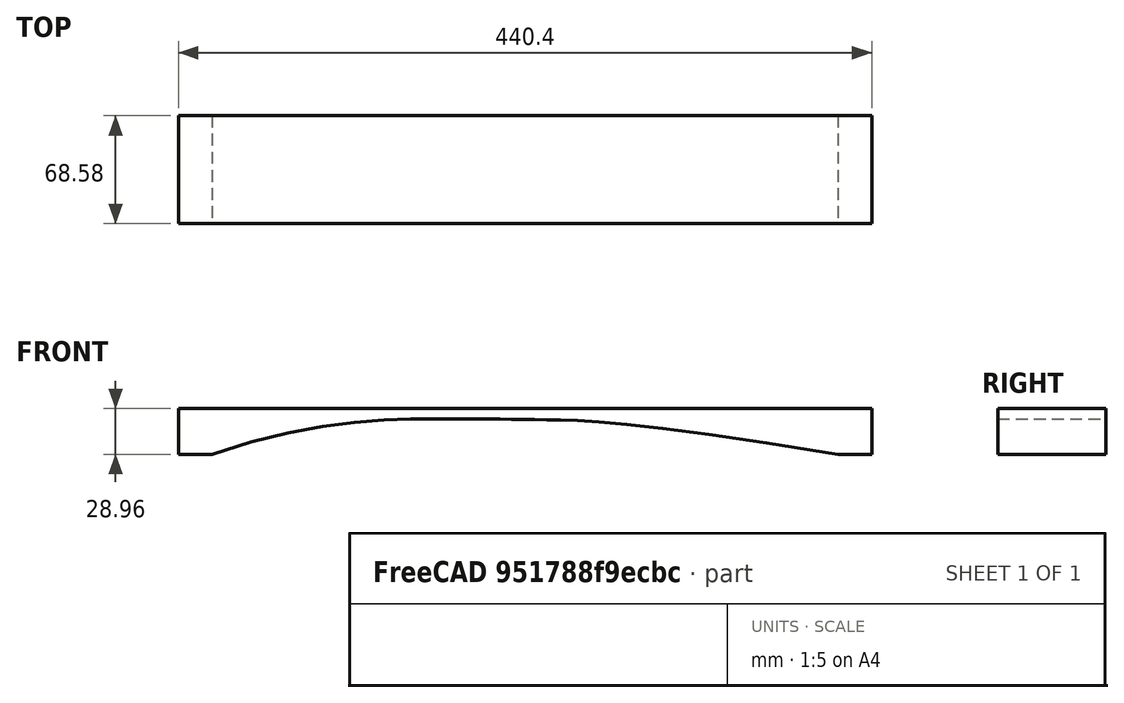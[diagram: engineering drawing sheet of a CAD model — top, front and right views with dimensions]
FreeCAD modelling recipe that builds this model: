
FCSTD DOCUMENT  (FreeCAD 0.20R29410 (Git))
Label: Single_Bar1
License: All rights reserved
LicenseURL: http://en.wikipedia.org/wiki/All_rights_reserved
objects: Fem::FemResultObjectPython×6, Sketcher::SketchObject×1, Part::Extrusion×1, Fem::FemSolverObjectPython×1, App::MaterialObjectPython×1, Fem::ConstraintDisplacement×1, Fem::FemMeshShapeNetgenObject×1, Fem::FemMeshObjectPython×1, App::TextDocument×1, Fem::FemAnalysis×1
note: 2 computed .brp shape members not serialized (recipe doc carries the construction recipe); baked Part::Feature solids carry a one-line shape summary decoded from their .brp

FEATURE [Sketcher::SketchObject] Sketch
  FullyConstrained = true
  Placement = pos=(0,0,0) rot=(1,0,0;1.5708rad)
  sketch-geometry (12):
    g0: LineSegment StartX=21.4 StartY=0 StartZ=0 EndX=0 EndY=0 EndZ=0
    g1: LineSegment StartX=0 StartY=0 StartZ=0 EndX=0 EndY=28.96 EndZ=0
    g2: LineSegment StartX=0 StartY=28.96 StartZ=0 EndX=440.4 EndY=28.96 EndZ=0
    g3: LineSegment StartX=440.4 StartY=28.96 StartZ=0 EndX=440.4 EndY=0 EndZ=0
    g4: LineSegment StartX=440.4 StartY=0 StartZ=0 EndX=419 EndY=0 EndZ=0
    g5-g10: Circle x6 (B-spline internal-alignment scaffolding for g11; pole/knot coordinates omitted)
    g11: BSplineCurve PolesCount=6 KnotsCount=4 Degree=3 IsPeriodic=0
  constraints (38):
    c: DistanceX(g0) = 0
    c: DistanceY(g0) = 0
    c: Distance(g1,g1) = 28.96
    c: Distance(g2,g2) = 440.4
    c: DistanceX(g0,g0) = 21.4
    c: DistanceX(g4,g4) = 21.4
    c: Horizontal(g0)
    c: Vertical(g1)
    c: Horizontal(g2)
    c: Vertical(g3)
    c: Horizontal(g4)
    c: Equal(g3,g1)
    c: Coincident(g0,g1)
    c: Coincident(g1,g2)
    c: Coincident(g2,g3)
    c: Coincident(g3,g4)
    c: DistanceX(g6) = 290.99
    c: DistanceY(g6) = 21.03
    c: DistanceX(g7) = 226.23
    c: DistanceY(g7) = 22.06
    c: DistanceX(g8) = 192.2
    c: DistanceY(g8) = 22.52
    c: DistanceX(g9) = 86.07
    c: DistanceY(g9) = 22.85
    c: Weight(g5) = 1
    c: InternalAlignment(g5,g11)
    c: Weight(g6) = 1
    c: InternalAlignment(g6,g11)
    c: Weight(g7) = 1
    c: InternalAlignment(g7,g11)
    c: Weight(g8) = 1
    c: InternalAlignment(g8,g11)
    c: Weight(g9) = 1
    c: InternalAlignment(g9,g11)
    c: Weight(g10) = 1
    c: InternalAlignment(g10,g11)
    c: Coincident(g4,g11)
    c: Coincident(g0,g11)
FEATURE [Part::Extrusion] Bar
  Base = -> Sketch
  Dir = (0,-1,-3e-16)
  DirMode = 2
  FaceMakerClass = Part::FaceMakerBullseye
  LengthFwd = 68.58
  LengthRev = 0
  Solid = true
  Symmetric = false
FEATURE [Fem::FemSolverObjectPython] SolverCcxTools  # FEM object (typed FeaturePython)
  AnalysisType = 1
  BeamShellResultOutput3D = false
  BucklingFactors = 1
  EigenmodeHighLimit = 20000
  EigenmodeLowLimit = 20
  EigenmodesCount = 12
  GeometricalNonlinearity = 0
  IterationsControlParameterCutb = 0.25,0.5,0.75,0.85,,,1.5,
  IterationsControlParameterIter = 4,8,9,200,10,400,,200,,
  IterationsControlParameterTimeUse = false
  IterationsThermoMechMaximum = 2000
  IterationsUserDefinedIncrementations = false
  IterationsUserDefinedTimeStepLength = false
  MaterialNonlinearity = 0
  MatrixSolverType = 0
  SplitInputWriter = false
  ThermoMechSteadyState = false
  TimeEnd = 1
  TimeInitialStep = 0.01
FEATURE [App::MaterialObjectPython] MaterialSolid  # material (typed FeaturePython)
  Category = 0
  Material = CompressiveStrength=4300 kPa; Density=430 kg/m^3; Name=Wood-Chestnut; PoissonRatio=0.32; ShearModulus=7.4 MPa; UltimateTensileStrength=59.0 MPa; YoungsModulus=8500 MPa
FEATURE [Fem::ConstraintDisplacement] FemConstraintDisplacement
  NormalDirection = (0,3e-16,-1)
  Normals = (110) [(0,3.3e-16,-1),(0,3.3e-16,-1),(0,3.3e-16,-1),(0,3.3e-16,-1),(0,3.3e-16,-1),(0,3.3e-16,-1),(0,3.3e-16,-1),(0,3.3e-16,-1),(0,3.3e-16,-1),(0,3.3e-16,-1),+100 more]
  Points = (110) [(21.4,-68.58,-2.26314e-14),(10.7,-68.58,-2.26314e-14),(0,-68.58,-2.26314e-14),(21.4,-45.72,-1.50876e-14),(10.7,-45.72,-1.50876e-14),+105 more]
  References = -> [Bar]
  rotxFix = false
  rotxFree = true
  rotyFix = false
  rotyFree = true
  rotzFix = false
  rotzFree = true
  xDisplacement = 0
  xFix = false
  xFree = true
  xRotation = 0
  yDisplacement = 0
  yFix = false
  yFree = true
  yRotation = 0
  zDisplacement = 0
  zFix = false
  zFree = true
  zRotation = 0
FEATURE [Fem::FemMeshShapeNetgenObject] FEMMeshNetgen
  Fineness = 4
  GrowthRate = 0.3
  MaxSize = 10
  NbSegsPerEdge = 1
  NbSegsPerRadius = 2
  Optimize = true
  SecondOrder = true
  Shape = -> Bar
FEATURE [Fem::FemMeshObjectPython] ResultMesh  # FEM object (typed FeaturePython)
FEATURE [Fem::FemResultObjectPython] CCX_EigenMode_7_Results  # FEM object (typed FeaturePython)
  DisplacementLengths = [73.6692,73.6675,97.3071,97.3053,92.9945,92.9927,105.905,105.905,112.704,112.704,83.0528,83.0531,92.865,102.962,108.891,106.382,90.7255,75.6183,60.5227,45.387,30.3859,15.6492,4.90783,16.1413,30.7596,45.472,60.0482,74.139,87.5335,99.8965,+5916 more]
  DisplacementVectors = (5946) [(-29.0771,-0.00393964,-67.6881),(-29.0769,0.00473664,-67.6863),(-29.0781,-0.00174479,-92.8608),(-29.0779,0.00241242,-92.859),+5942 more]
  Eigenmode = 7
  EigenmodeFrequency = 127.893
  MaxShear = [0.52739,0.591867,0.0506016,0.0460882,0.0804371,0.098039,0.114135,0.0877355,0.0556531,0.0486395,0.404434,0.419503,0.296947,0.119579,0.178383,0.158839,0.229624,0.660296,1.49302,3.05771,6.05637,10.0987,19.8211,30.5738,45.3514,66.0593,93.6442,+5919 more]
  Mesh = -> ResultMesh
  NodeNumbers = [1,2,3,4,5,6,7,8,9,10,11,12,13,14,15,16,17,18,19,20,21,22,23,24,25,26,27,28,29,30,31,32,33,34,35,36,37,38,39,40,41,42,43,44,45,46,47,48,49,50,51,52,53,54,55,56,57,58,59,60,61,62,63,64,65,66,67,68,69,+5877 more]
  NodeStrainXX = [-0.000119642,-0.000131516,2.52116e-06,2.57943e-06,1.81851e-06,3.90222e-06,3.5195e-07,2.12321e-06,2.36053e-06,2.35781e-06,-8.34904e-05,-8.33955e-05,-5.91647e-05,-1.96769e-05,-7.4614e-06,8.23758e-06,9.19814e-06,0.00010886,0.000271382,+5927 more]
  NodeStrainXY = [1.83996e-05,-1.9545e-05,-1.7626e-06,1.03443e-06,5.54064e-07,-3.24496e-06,-5.29428e-06,4.305e-06,2.33814e-06,-1.72162e-06,-1.79782e-05,1.96224e-05,-2.0511e-05,-5.62808e-06,4.21188e-06,-3.79588e-06,3.11899e-05,5.66166e-05,0.000107873,+5927 more]
  NodeStrainXZ = [3.21037e-06,-1.50244e-05,5.57866e-06,5.33098e-06,9.98465e-06,1.32757e-05,-1.28022e-05,-1.10483e-05,-5.3965e-06,-4.58391e-06,-1.41902e-05,-1.31345e-05,1.46026e-05,9.52499e-06,1.62342e-05,2.01921e-05,1.6494e-05,4.89176e-05,9.8758e-05,+5927 more]
  NodeStrainYY = [3.4399e-05,4.18475e-05,-5.24387e-06,-4.38816e-06,6.40805e-06,2.50142e-06,9.75058e-06,5.85631e-06,-6.33621e-06,-5.57897e-06,2.82298e-05,2.74828e-05,7.81986e-06,2.57164e-06,-8.32709e-06,1.18314e-06,-1.85328e-06,-2.94223e-05,-8.89012e-05,+5927 more]
  NodeStrainYZ = [5.58355e-07,1.00263e-06,2.27123e-06,-2.4793e-06,1.69937e-06,-2.56722e-06,2.70199e-06,-6.16798e-07,3.03519e-06,-3.16863e-06,-7.55747e-06,1.11874e-05,6.30026e-06,7.55929e-06,-1.57843e-05,-1.0551e-05,1.14837e-06,4.00297e-06,-1.18752e-07,+5927 more]
  NodeStrainZZ = [4.17109e-05,4.62749e-05,3.57609e-06,2.83123e-06,-1.13761e-05,-7.69219e-06,-1.26095e-05,-8.24806e-06,4.0092e-06,3.07161e-06,3.11042e-05,3.28491e-05,2.13049e-05,5.00867e-06,1.98025e-05,-9.0146e-06,-2.89223e-06,-4.03627e-05,-8.76131e-05,+5927 more]
  NodeStressXX = [-1.0196,-1.09527,0.0211194,0.0224626,-0.0063175,0.0177524,-0.0120836,0.0121351,0.0153923,0.0143268,-0.675897,-0.669031,-0.552931,-0.195948,-0.0250714,0.0553697,0.0847169,0.924648,2.29055,5.09357,10.1495,17.5392,27.8086,46.7294,74.3148,+5921 more]
  NodeStressXY = [0.118482,-0.125858,-0.01135,0.00666108,0.00356784,-0.0208956,-0.034092,0.0277216,0.0150562,-0.0110862,-0.115769,0.126356,-0.132078,-0.0362414,0.027122,-0.0244432,0.200844,0.364576,0.694634,1.18076,2.10425,3.74355,6.51758,10.023,14.613,+5921 more]
  NodeStressXZ = [0.0206729,-0.0967478,0.0359232,0.0343283,0.0642951,0.0854874,-0.0824386,-0.0711446,-0.0347502,-0.0295176,-0.0913761,-0.0845783,0.0940317,0.0613352,0.104538,0.130025,0.106211,0.315,0.635942,1.09413,2.51491,2.89219,13.6365,18.3075,23.4376,+5921 more]
  NodeStressYY = [-0.027666,0.0210892,-0.0288827,-0.0224044,0.0232363,0.00873208,0.0484379,0.036174,-0.0406095,-0.0367813,0.0435135,0.0449586,-0.121591,-0.0526801,-0.0306459,0.00994338,0.0135524,0.0341973,-0.0294533,-0.0223564,-0.196566,-0.432321,-0.462682,+5923 more]
  NodeStressYZ = [0.00359547,0.00645634,0.0146253,-0.0159652,0.0109429,-0.0165313,0.0173991,-0.0039718,0.0195448,-0.020404,-0.0486655,0.0720403,0.0405699,0.0486773,-0.101641,-0.0679419,0.00739482,0.0257767,-0.000764693,-0.0764151,0.0624407,0.0309516,+5924 more]
  NodeStressZZ = [0.0194184,0.0495988,0.0279125,0.0240841,-0.0912828,-0.0569086,-0.0955478,-0.0546496,0.0260087,0.0189232,0.0620233,0.0795143,-0.0347548,-0.0369871,0.150491,-0.0557239,0.00686225,-0.0362525,-0.021159,-0.0372765,-0.0100599,-0.109105,2.5853,+5923 more]
  PrincipalMax = [0.0208401,0.0666409,0.0607182,0.0582064,0.0345879,0.0831687,0.0820056,0.0746249,0.0561383,0.0469651,0.102327,0.136535,-0.0142484,0.00784923,0.22615,0.163847,0.281082,1.13484,2.62506,5.55164,11.1148,18.7172,34.8505,54.9825,83.7173,124.566,+5920 more]
  PrincipalMed = [-0.014748,0.0258694,-8.4104e-05,-9.41236e-05,0.0173345,-0.00068365,0.00506526,0.0198806,-0.000178905,-0.00018246,0.0338542,0.0213786,-0.0868855,-0.0621556,-0.000761002,-0.000427838,0.00221562,-0.0264947,-0.0241364,0.046074,-0.173919,+5925 more]
  PrincipalMin = [-1.03394,-1.11709,-0.0404849,-0.03397,-0.126286,-0.112909,-0.146264,-0.100846,-0.0551679,-0.0503139,-0.706541,-0.702471,-0.608143,-0.231309,-0.130615,-0.15383,-0.178166,-0.185752,-0.360982,-0.563775,-0.99797,-1.48028,-4.79169,-6.16515,+5922 more]
  ResultType = Fem::ResultMechanical
  Stats = [-29.0786,38.8721,-0.614078,0.614148,-105.797,138.484,1.01682,138.485,0.0483488,534.322,-5.05672,536.125,-45.106,43.424,-533.32,5.80692,0.0277996,268.015,0,0,0,0,0,0,0,0]
  Time = 0
  vonMises = [1.03744,1.16388,0.0882362,0.0807558,0.152979,0.1704,0.201156,0.155502,0.0963963,0.0842593,0.776899,0.787766,0.561113,0.212967,0.312755,0.275171,0.400757,1.2486,2.83268,5.83444,11.7225,19.6064,37.5282,58.521,87.6023,128.655,183.703,252.313,+5918 more]
FEATURE [Fem::FemResultObjectPython] CCX_EigenMode_8_Results  # FEM object (typed FeaturePython)
  DisplacementLengths = [119.986,119.986,118.425,118.426,121.101,121.101,158.735,158.736,166.556,166.557,168.038,168.038,167.542,167.037,153.79,149.763,158.067,157.396,156.692,155.921,155.039,153.958,152.576,150.699,148.092,144.393,139.126,131.843,122.106,109.748,+5916 more]
  DisplacementVectors = (5946) [(-7.21104,47.4306,-109.977),(7.21118,47.4302,109.977),(-7.20026,43.0029,-110.106),(7.20047,43.003,110.107),(-7.05204,-49.9225,-110.107),+5941 more]
  Eigenmode = 8
  EigenmodeFrequency = 439.297
  MaxShear = [6.8768,6.58187,0.632806,0.536714,1.17289,1.33832,1.77202,1.97638,1.05325,1.03926,11.0362,11.2586,7.76355,1.93396,2.65948,2.13644,5.42117,17.6965,32.4332,51.968,77.6808,109.095,147.625,207.062,278.162,363.628,460.209,560.188,653.493,731.262,+5916 more]
  Mesh = -> ResultMesh
  NodeNumbers = <same value as first occurrence — deduplicated (x6 in doc)>
  NodeStrainXX = [0.00147502,-0.00137483,-4.237e-05,4.01089e-05,5.94362e-05,-0.000125532,-0.000118239,0.000232046,7.28825e-05,-7.48978e-05,-0.00236143,0.00240008,-0.0016599,-0.000307137,0.000124711,-0.000120344,0.00104086,0.00397285,0.00746572,0.0119311,+5926 more]
  NodeStrainXY = [0.000256139,0.00032677,-5.96381e-05,-5.15006e-05,6.27801e-05,9.4798e-05,9.09463e-05,0.000166946,-9.95497e-05,-0.000104641,0.000228171,0.000279948,0.000463923,0.000153508,-0.000192135,6.58666e-05,-0.00048798,-0.000698514,-0.000985615,+5927 more]
  NodeStrainXZ = [-0.000366522,0.000420505,9.7992e-06,-4.69516e-06,1.16612e-05,-4.07534e-06,-2.02916e-05,4.3949e-05,-4.85588e-06,1.85302e-05,-0.000783191,0.000799228,-0.000148369,-3.62534e-06,7.77145e-05,0.000153981,-0.00012439,-0.000335253,-0.000537179,+5927 more]
  NodeStrainYY = [-0.000524213,0.00046216,-2.1911e-05,1.94842e-05,8.24434e-05,-4.6769e-05,-8.81564e-05,8.02871e-06,3.16639e-05,-3.19969e-05,0.000832215,-0.000852385,0.000554741,4.45459e-05,0.000201236,-9.38033e-05,-0.000210064,-0.00131068,-0.00238061,+5927 more]
  NodeStrainYZ = [-2.74103e-05,-7.00243e-05,-5.23691e-05,-4.11819e-05,-0.000112998,-9.64257e-05,0.000186304,0.000134041,9.4919e-05,9.06935e-05,7.14911e-05,6.56695e-05,2.91389e-05,0.000157755,-0.00023188,-0.000190993,0.000133404,8.38006e-05,3.83965e-05,+5927 more]
  NodeStrainZZ = [-0.00041494,0.000404234,6.51988e-05,-5.64535e-05,-0.000156871,0.000179907,0.000218563,-0.000205895,-9.71746e-05,8.65484e-05,0.000638462,-0.000657409,0.000499118,4.89714e-05,-0.000304239,0.000273818,-0.00035197,-0.00121193,-0.0023669,+5927 more]
  NodeStressXX = [12.5655,-11.7633,-0.267583,0.276248,0.296923,-0.764811,-0.691746,1.68987,0.511514,-0.598756,-20.3048,20.551,-14.1577,-3.20051,0.927319,-0.433396,9.44331,33.8838,63.6334,101.622,150.013,210.337,259.761,355.381,462.076,575.766,677.793,+5919 more]
  NodeStressXY = [1.64938,2.1042,-0.384033,-0.331633,0.404266,0.610442,0.585639,1.07503,-0.64104,-0.673826,1.46928,1.8027,2.98739,0.988499,-1.23724,0.424141,-3.1423,-4.49801,-6.34676,-9.88515,-18.2624,-29.5205,-54.1298,-83.3151,-123.951,-181.311,-258.465,+5919 more]
  NodeStressXZ = [-2.36018,2.7078,0.0631009,-0.030234,0.0750911,-0.0262427,-0.130665,0.283005,-0.0312689,0.119324,-5.04327,5.14655,-0.955409,-0.023345,0.500435,0.991545,-0.800995,-2.15882,-3.4591,-7.21763,-10.7556,-15.6809,-36.6852,-54.1967,-80.3852,+5921 more]
  NodeStressYY = [-0.308374,0.0658042,-0.13584,0.143438,0.445075,-0.257625,-0.498029,0.247339,0.246092,-0.322501,0.260378,-0.392939,0.103276,-0.935889,1.42009,-0.262488,1.3881,-0.138932,0.229028,0.221337,0.923959,3.14973,3.48502,3.72324,6.00106,9.09407,+5920 more]
  NodeStressYZ = [-0.176506,-0.450914,-0.337225,-0.265186,-0.727638,-0.620923,1.19968,0.863142,0.611221,0.584011,0.46036,0.422872,0.187637,1.01584,-1.49317,-1.22988,0.859039,0.539625,0.24725,0.393437,-0.0313053,0.913457,-4.73871,-7.83643,-10.3208,-12.8632,+5920 more]
  NodeStressZZ = [0.395277,-0.307205,0.425095,-0.345555,-1.09596,1.20203,1.47706,-1.1302,-0.58355,0.440859,-0.987279,0.862587,-0.254906,-0.907392,-1.83486,2.10477,0.474309,0.496955,0.317345,0.427772,-0.106044,-0.478904,-4.68117,-5.81872,-7.1373,-8.48965,+5920 more]
  PrincipalMax = [13.2095,0.430853,0.643733,0.572797,0.931538,1.45734,2.04998,2.39062,1.14005,0.798988,0.422462,21.9684,0.703809,0.237721,2.90281,2.80926,10.6303,34.6116,64.4499,103.085,152.962,215.596,275.115,380.905,504.719,646.75,794.824,926.416,1015.04,+5917 more]
  PrincipalMed = [-0.013016,0.297326,-0.00018087,0.00196622,0.128748,-0.0584483,-0.268626,-0.0214717,0.000446333,0.000139868,0.195806,-0.399028,-0.189855,-1.65131,0.0259041,0.0632434,0.88754,0.411625,0.146473,0.0375826,0.268785,0.0075643,3.58593,5.59854,+5922 more]
  PrincipalMin = [-0.544087,-12.7329,-0.62188,-0.500632,-1.41425,-1.2193,-1.49407,-1.56214,-0.966445,-1.27953,-21.65,-0.548772,-14.8233,-3.63021,-2.41616,-1.46362,-0.212078,-0.781443,-0.416553,-0.851231,-2.39974,-2.59528,-20.1358,-33.2182,-51.6041,-80.5063,+5920 more]
  ResultType = Fem::ResultMechanical
  Stats = [-9.52769,9.53894,-76.8829,53.0045,-149.509,149.508,0.715849,168.038,0.731194,1951.35,-4.00669,1208.44,-31.344,30.6989,-1195.38,5.40699,0.407832,1126.6,0,0,0,0,0,0,0,0]
  Time = 0
  UserDefined = [13.7536,13.1637,1.26561,1.07343,2.34579,2.67663,3.54405,3.95275,2.1065,2.07851,22.0724,22.5172,15.5271,3.86793,5.31897,4.27288,10.8423,35.3931,64.8664,103.936,155.362,218.191,295.251,414.123,556.323,727.256,920.417,1120.38,1306.99,1462.52,+5916 more]
  vonMises = [13.4959,13.0975,1.09611,0.930242,2.06495,2.32482,3.11752,3.4508,1.82633,1.81603,21.96,22.4427,15.1001,3.35003,4.61149,3.75029,10.3365,34.8119,64.5867,103.494,154.045,216.901,284.133,396.144,529.118,686.442,859.815,1032.53,1184.51,1301.8,+5916 more]
FEATURE [Fem::FemResultObjectPython] CCX_EigenMode_9_Results  # FEM object (typed FeaturePython)
  DisplacementLengths = [54.826,54.8154,83.8163,83.8058,82.2506,82.2408,94.1647,94.1621,103.38,103.378,64.9392,64.9376,76.911,90.1383,96.4824,92.7828,72.7188,51.7462,31.946,17.8081,23.8765,41.9659,62.0764,82.3777,101.936,120.086,135.924,148.035,155.01,155.43,+5916 more]
  DisplacementVectors = (5946) [(24.0545,0.0484573,49.2673),(24.0528,-0.053128,49.2563),(24.0678,0.0224879,80.2864),(24.0669,-0.0259825,80.2758),(-17.8669,-0.0257076,80.2866),+5941 more]
  Eigenmode = 9
  EigenmodeFrequency = 517.454
  MaxShear = [7.19366,7.9243,0.645035,0.589606,1.05677,1.2851,1.36954,1.04997,0.64048,0.561347,6.29245,6.44647,4.46465,1.71954,2.09113,1.89825,2.69423,9.49926,20.8265,40.8414,74.7701,118.968,197.289,289.77,403.228,544.669,706.967,872.733,1011.26,1081.85,+5916 more]
  Mesh = -> ResultMesh
  NodeNumbers = <same value as first occurrence — deduplicated (x6 in doc)>
  NodeStrainXX = [0.00164125,0.00177629,-3.08728e-05,-3.13733e-05,-2.93827e-05,-5.29212e-05,1.28785e-05,1.8107e-05,2.48319e-05,2.53805e-05,-0.00133744,-0.00133909,-0.000968663,-0.000329513,-9.15943e-05,9.91222e-05,0.000298276,0.00189847,0.004328,0.00878484,+5926 more]
  NodeStrainXY = [-0.000222711,0.000229767,2.21933e-05,-1.376e-05,-4.51733e-06,3.68019e-05,-5.46873e-05,4.0375e-05,2.55339e-05,-1.83743e-05,-0.00018214,0.000196759,-0.000202327,-6.30377e-05,3.72653e-05,-3.7669e-05,0.000323521,0.000580579,0.00106025,+5927 more]
  NodeStrainXZ = [-6.33551e-05,0.000163835,-7.20874e-05,-6.86863e-05,-0.000131105,-0.000175409,-0.000158099,-0.000139922,-6.43528e-05,-5.47883e-05,-0.000277525,-0.000267383,0.000159465,0.000113773,0.000192218,0.000241678,0.000184488,0.000533279,0.00103712,+5927 more]
  NodeStrainYY = [-0.000485226,-0.000562283,6.61739e-05,5.60823e-05,-8.1851e-05,-3.15787e-05,0.000111921,6.85868e-05,-7.11427e-05,-6.29853e-05,0.000457357,0.000449601,0.000195339,7.0874e-05,-9.77664e-05,1.79344e-05,-8.84041e-05,-0.000557485,-0.00141145,+5927 more]
  NodeStrainYZ = [4.93019e-07,-1.58631e-05,-2.72614e-05,3.03896e-05,-1.76138e-05,2.8339e-05,2.51152e-05,-4.08648e-06,3.18281e-05,-3.47276e-05,-8.79435e-05,0.000126475,5.9735e-05,7.6048e-05,-0.000176666,-0.000121083,7.88856e-06,2.99812e-05,-1.90956e-05,+5927 more]
  NodeStrainZZ = [-0.000565771,-0.000626256,-4.78106e-05,-3.84883e-05,0.000155529,0.000104951,-0.000163657,-0.000100407,5.04993e-05,3.87813e-05,0.000467652,0.000487903,0.000334966,8.8635e-05,0.000254418,-0.00012134,-9.42359e-05,-0.00066772,-0.00138982,+5927 more]
  NodeStressXX = [13.9472,14.8025,-0.270406,-0.280897,0.0643377,-0.223722,-0.139489,0.0381034,0.183877,0.170169,-10.973,-10.9216,-8.74673,-3.09495,-0.217429,0.613772,2.58261,16.0788,36.6085,74.4322,136.325,221.62,323.184,501.096,730.944,1022.68,1364.09,+5919 more]
  NodeStressXY = [-1.43413,1.47956,0.142911,-0.0886062,-0.0290889,0.236982,-0.352153,0.259991,0.164423,-0.118319,-1.17287,1.26701,-1.30286,-0.405924,0.239966,-0.242566,2.08328,3.73857,6.82735,11.0372,18.2412,30.2147,49.3568,69.3973,91.561,111.767,123.754,+5919 more]
  NodeStressXZ = [-0.407969,1.055,-0.464199,-0.442298,-0.844236,-1.12953,-1.01806,-0.901014,-0.414393,-0.352803,-1.78709,-1.72179,1.02686,0.732628,1.23777,1.55626,1.18799,3.43399,6.67844,10.7305,23.8866,24.9251,116.425,143.467,165.513,180.804,180.279,157.12,+5918 more]
  NodeStressYY = [0.254001,-0.256529,0.354516,0.282264,-0.273526,-0.0862886,0.498284,0.363163,-0.434141,-0.398853,0.584389,0.596496,-1.25126,-0.516702,-0.257173,0.0909718,0.0926212,0.263866,-0.349998,-0.371983,-1.65969,-3.80126,-1.78117,-1.97116,0.288604,+5921 more]
  NodeStressYZ = [0.00317475,-0.102149,-0.175547,0.195691,-0.113422,0.182486,0.161727,-0.0263144,0.204954,-0.223624,-0.566303,0.814424,0.384657,0.489703,-1.13762,-0.779702,0.0507976,0.193061,-0.122964,-0.853303,0.220227,0.000548324,4.20607,5.6384,6.57102,+5921 more]
  NodeStressZZ = [-0.26466,-0.668477,-0.379475,-0.326713,1.25506,0.792879,-1.27627,-0.725057,0.349159,0.256462,0.650681,0.843138,-0.352148,-0.402331,2.01068,-0.805869,0.0550679,-0.445978,-0.210705,-0.3745,-0.196789,-1.4965,22.6644,16.8128,17.9026,16.772,+5920 more]
  PrincipalMax = [14.1073,15.0155,0.496542,0.425913,1.69662,1.52359,0.864573,0.769108,0.691873,0.577568,1.21377,1.56675,-0.17001,0.0637587,2.85868,1.84735,4.04908,17.5581,38.9276,77.4443,142.635,228.258,369.242,548.909,778.099,1065.88,1398.76,1738.28,+5918 more]
  PrincipalMed = [0.109332,-0.304881,0.00162204,0.0020387,-0.23384,0.00588034,0.0924651,0.23794,-0.00389054,-0.00466526,0.419425,0.277473,-1.08081,-0.702426,0.000990845,0.00065943,0.0206089,-0.220924,-0.154243,0.479818,-1.26129,-2.25876,0.159718,-2.33964,+5922 more]
  PrincipalMin = [-0.280056,-0.833109,-0.793529,-0.753298,-0.41691,-1.04661,-1.87451,-1.33084,-0.589087,-0.545125,-11.3711,-11.3262,-9.09932,-3.37532,-1.32359,-1.94914,-1.33939,-1.44045,-2.72553,-4.2384,-6.90519,-9.67706,-25.3349,-30.6317,-28.3568,-23.4602,+5920 more]
  ResultType = Fem::ResultMechanical
  Stats = [-17.8701,46.0124,-1.86934,1.86731,-116.978,156.053,0.831568,156.224,0.622299,2147.23,-24.9315,2161.96,-330.761,318.014,-2144.3,32.6406,0.356801,1085.5,0,0,0,0,0,0,0,0]
  Time = 0
  vonMises = [14.1966,15.5912,1.12727,1.03459,2.0282,2.23798,2.4462,1.89116,1.11072,0.972505,12.2071,12.2991,8.51054,3.12719,3.70218,3.28826,4.85354,18.4191,40.4288,79.4288,146.8,234.314,382.468,565.925,792.945,1077.26,1404.36,1736.34,2008.35,2143.76,+5916 more]
FEATURE [Fem::FemResultObjectPython] CCX_EigenMode_10_Results  # FEM object (typed FeaturePython)
  DisplacementLengths = [76.2192,76.2182,98.9648,98.9639,115.566,115.566,128.799,128.798,102.171,102.168,79.835,79.8335,86.7825,94.4275,109.813,118.659,116.197,104.071,92.5148,81.7473,72.2181,64.3434,58.7281,55.8455,55.9688,58.8698,64.0466,70.8439,78.7046,87.0527,+5916 more]
  DisplacementVectors = (5946) [(44.4024,57.8037,22.283),(-44.401,57.8039,-22.2816),(44.4139,85.5424,22.4483),(-44.4132,85.5423,-22.4463),(44.1858,104.397,22.4577),+5941 more]
  Eigenmode = 10
  EigenmodeFrequency = 1114.62
  MaxShear = [7.02165,7.3129,0.625801,0.522768,3.29847,4.47889,4.95916,5.63025,1.36168,1.38004,9.65909,10.4723,7.34647,4.69604,3.10374,5.60564,14.3619,53.323,105.029,173.904,262.269,364.688,496.131,648.998,814.437,986.97,1153.82,1298.77,1413.38,1501.29,+5916 more]
  Mesh = -> ResultMesh
  NodeNumbers = <same value as first occurrence — deduplicated (x6 in doc)>
  NodeStrainXX = [0.00136374,-0.00145839,4.62407e-05,-4.53288e-05,-0.000192482,0.000382576,-0.000336682,0.000673931,0.000123602,-0.000129686,-0.00184741,0.00195683,-0.00110578,0.000100109,0.000116055,-0.000380575,0.00309335,0.0121943,0.0244241,0.0405467,+5926 more]
  NodeStrainXY = [-0.00052207,-0.000384411,-3.04978e-05,-6.23019e-06,-0.000271578,-0.000504267,0.000383017,0.000557847,-6.05385e-05,-8.72441e-05,0.000579255,0.000678504,0.000885837,0.000625294,-9.98436e-05,0.000262202,-0.000740143,-0.00136898,-0.0021695,+5927 more]
  NodeStrainXZ = [3.69665e-05,-0.000220017,3.46429e-05,-5.07515e-05,-3.26497e-05,1.40395e-05,-2.27621e-05,7.54134e-05,-6.62314e-05,9.95628e-05,-0.000768293,0.000837972,-0.000298431,-0.000118687,0.000107478,0.00029065,-0.000196906,-0.000808819,-0.00126852,+5927 more]
  NodeStrainYY = [-0.000461521,0.000439887,-8.05557e-05,5.1194e-05,-0.000251186,0.00021801,-0.000301738,8.67145e-05,-7.35616e-05,5.71523e-05,0.000660458,-0.000705623,0.000242361,-0.000212833,5.36063e-05,-0.000339461,-0.000778218,-0.00405338,-0.00784809,+5927 more]
  NodeStrainYZ = [0.000113862,0.00010933,6.69562e-05,4.01166e-05,0.000213106,0.000188128,0.000401769,0.000288184,0.000156709,0.000136404,0.000179096,0.000161646,0.000138601,0.000333274,-0.000435484,-0.000335376,0.000276418,0.000198045,0.000124466,+5927 more]
  NodeStrainZZ = [-0.000495117,0.00059468,-7.6909e-08,-8.56089e-06,0.00042922,-0.000496782,0.000604714,-0.000588935,-6.43117e-05,4.17856e-05,0.000416193,-0.000477758,0.000360339,-8.4078e-05,-0.000175345,0.000875315,-0.00101856,-0.00377454,-0.00776179,+5927 more]
  NodeStressXX = [11.1119,-11.8171,0.100906,-0.307319,-1.32217,3.05772,-2.36096,5.32256,0.714234,-1.0111,-16.3079,17.028,-10.0001,-0.48183,0.714789,-1.56187,27.3407,103.517,207.728,345.152,519.998,724.208,956.915,1249.88,1564.25,1890.88,2207.13,2485.68,+5918 more]
  NodeStressXY = [-3.36181,-2.47537,-0.196387,-0.0401187,-1.7488,-3.24717,2.4664,3.5922,-0.389831,-0.561799,3.73005,4.36915,5.70425,4.02652,-0.642932,1.68842,-4.76607,-8.81539,-13.9703,-19.8182,-33.5159,-49.697,-86.0763,-119.751,-159.054,-203.334,-247.582,+5919 more]
  NodeStressXZ = [0.238042,-1.41678,0.223079,-0.326809,-0.210244,0.0904056,-0.146574,0.485616,-0.42649,0.641124,-4.94734,5.39603,-1.92171,-0.76427,0.692094,1.87161,-1.26796,-5.2083,-8.16851,-15.2356,-21.8907,-26.7799,-70.8296,-92.5163,-120.826,-152.009,+5920 more]
  NodeStressYY = [-0.641692,0.406682,-0.715585,0.314229,-1.70019,1.99802,-2.13594,1.54124,-0.55538,0.192026,-0.158793,-0.11661,-1.3189,-2.49699,0.312658,-1.29712,2.41016,-1.10856,-0.0852899,0.621013,1.35149,5.95576,2.58203,2.18296,2.04041,1.22315,-1.16515,+5919 more]
  NodeStressYZ = [0.733205,0.704019,0.431157,0.258327,1.37227,1.21143,2.58715,1.85573,1.00911,0.878357,1.15327,1.04091,0.892503,2.14608,-2.80426,-2.15962,1.77997,1.27529,0.801482,1.48392,1.0302,2.2151,-4.2851,-7.26027,-9.29572,-10.9766,-11.7121,-11.099,+5918 more]
  NodeStressZZ = [-0.858031,1.40345,-0.197351,-0.0705565,2.68122,-2.60481,3.70106,-2.80953,-0.495816,0.0930745,-1.73171,1.3507,-0.559195,-1.66789,-1.16165,6.5253,0.86248,0.68699,0.470444,0.95816,-0.333561,0.27912,-11.2458,-11.5452,-13.1857,-13.5665,-12.5061,+5919 more]
  PrincipalMax = [12.0057,2.21171,0.221835,0.492135,3.19237,5.87941,4.76746,7.67533,1.18807,1.02294,0.665485,19.7184,1.51008,2.79324,2.87724,7.31247,28.3109,104.525,208.986,346.964,523.072,728.622,969.636,1267.8,1589.16,1924.13,2248.61,2532.48,2761.38,+5917 more]
  PrincipalMed = [-0.355822,0.195418,-0.00409808,-0.00238057,-0.128931,-0.350109,-0.412436,-0.0358974,0.0102602,-0.0117948,-0.211191,-0.229956,-0.20542,-0.841127,0.318788,0.252653,2.71538,0.691884,0.200542,0.611094,-0.589868,2.57506,1.24156,2.90956,3.65638,+5921 more]
  PrincipalMin = [-2.03765,-12.4141,-1.02977,-0.553401,-3.40458,-3.07837,-5.15086,-3.58517,-1.53529,-1.73714,-18.6527,-1.22633,-13.1829,-6.59883,-3.33023,-3.89881,-0.412917,-2.12119,-1.07311,-0.844319,-1.4664,-0.753685,-22.6266,-30.194,-39.7127,-49.8148,+5920 more]
  ResultType = Fem::ResultMechanical
  Stats = [-49.9118,49.9103,-123.773,112.619,-38.2598,38.2643,0.528405,128.799,0.905902,4115.61,-15.4734,4118.61,-109.569,119.045,-4119.73,11.3021,0.522768,2059.8,0,0,0,0,0,0,0,0]
  Time = 0
  vonMises = [13.2825,13.7292,1.15533,0.905902,5.71317,7.95275,8.59235,9.97144,2.36566,2.41511,18.8951,20.4647,13.9147,8.20277,5.40341,9.81755,27.2944,105.268,209.425,347.083,524.101,727.717,980.547,1281.77,1607.63,1947.48,2276.84,2564.54,2794.3,2973.12,+5916 more]
FEATURE [Fem::FemResultObjectPython] CCX_EigenMode_11_Results  # FEM object (typed FeaturePython)
  DisplacementLengths = [48.4227,48.399,79.1734,79.1499,75.4207,75.3971,78.4911,78.4832,86.9854,86.9798,51.5983,51.5964,61.9331,74.2566,79.4823,75.8705,57.6304,37.9274,22.5145,22.9682,38.3324,56.9849,75.295,91.6826,104.398,111.357,109.928,97.4125,71.9486,34.2871,+5916 more]
  DisplacementVectors = (5946) [(29.7097,0.247689,38.2365),(29.7056,-0.264639,38.2095),(29.7889,0.111854,73.3556),(29.7891,-0.126206,73.3301),(-17.522,-0.136126,73.357),+5941 more]
  Eigenmode = 11
  EigenmodeFrequency = 1285.6
  MaxShear = [41.768,45.2412,3.379,3.09644,5.68449,6.8853,6.29792,4.82474,2.87575,2.52241,33.1101,33.7703,23.3186,8.85674,9.52198,8.73981,13.0541,49.1863,104.856,199.003,346.148,531.1,786.271,1098.22,1428.32,1771.17,2059.55,2189.5,2050.51,1597.22,969.4,+5915 more]
  Mesh = -> ResultMesh
  NodeNumbers = <same value as first occurrence — deduplicated (x6 in doc)>
  NodeStrainXX = [0.00957121,0.01023,-0.000156458,-0.000158053,-0.000181278,-0.000297808,-8.61308e-05,-6.74878e-05,-0.000103791,-0.000107901,0.00709724,0.00711186,0.00519362,0.00178952,0.000426737,-0.000456634,-0.00193903,-0.0104,-0.0227476,-0.0441477,+5926 more]
  NodeStrainXY = [-0.00112608,0.00113329,0.000114673,-7.39034e-05,-1.36066e-05,0.000176806,0.000227251,-0.000154609,-0.000110771,7.82676e-05,0.000748625,-0.000803003,0.000814811,0.000280452,-0.000135528,0.00015257,-0.00135664,-0.00240411,-0.00422875,+5927 more]
  NodeStrainXZ = [-0.000486776,0.000694915,-0.000381376,-0.000362293,-0.000701,-0.000941564,0.000737394,0.000661158,0.000295222,0.000251498,0.00156736,0.00152775,-0.000694253,-0.000526276,-0.000881627,-0.00111463,-0.00082025,-0.00231578,-0.00435483,+5927 more]
  NodeStrainYY = [-0.00289296,-0.0032352,0.000343909,0.000294196,-0.000429069,-0.000161157,-0.000499506,-0.000309451,0.000314103,0.00027882,-0.00243723,-0.00240463,-0.00118513,-0.000441219,0.000444421,-9.09546e-05,0.000603856,0.00313965,0.00740538,0.0142604,+5926 more]
  NodeStrainYZ = [3.4844e-05,-9.70835e-05,-0.000136707,0.000154907,-7.68213e-05,0.000132931,-9.59194e-05,9.69386e-06,-0.000133922,0.000150705,0.000395931,-0.000558912,-0.000232823,-0.000311318,0.000781794,0.000544295,-2.08781e-05,-9.07972e-05,0.000126872,+5927 more]
  NodeStrainZZ = [-0.00326348,-0.00359382,-0.000259111,-0.000211099,0.000857892,0.000579112,0.00078701,0.00046761,-0.000239608,-0.000184564,-0.0024172,-0.00250797,-0.00176676,-0.000490797,-0.00121659,0.00059045,0.000613179,0.00358327,0.00728248,0.0141811,+5926 more]
  NodeStressXX = [81.1786,85.3422,-1.41767,-1.44681,0.2496,-1.22999,0.59801,0.0844118,-0.836042,-0.772913,58.5396,58.3844,46.2752,16.4318,0.770713,-2.69511,-16.6188,-88.0166,-192.613,-374.185,-652.171,-1017.06,-1399.42,-2030.92,-2737.23,-3472.11,-4087.1,+5919 more]
  NodeStressXY = [-7.25126,7.29771,0.738423,-0.475893,-0.0876185,1.13853,1.46336,-0.995587,-0.713296,0.503996,4.82069,-5.17085,5.24689,1.80594,-0.872718,0.982459,-8.73596,-15.481,-27.2306,-42.1359,-64.7517,-99.1896,-150.712,-188.355,-213.294,-206.342,+5920 more]
  NodeStressXZ = [-3.13454,4.47483,-2.45583,-2.33295,-4.51402,-6.0631,4.74837,4.25745,1.90105,1.6195,10.0929,9.83777,-4.47057,-3.3889,-5.67714,-7.17751,-5.28191,-14.9122,-28.0425,-42.6842,-91.5367,-87.0676,-395.949,-440.683,-440.742,-391.047,-270.276,+5919 more]
  NodeStressYY = [0.916897,-1.36569,1.80438,1.4654,-1.34602,-0.350039,-2.06388,-1.47369,1.85494,1.71733,-2.85662,-2.89596,5.1999,2.06712,0.88459,-0.340354,-0.244133,-0.829649,1.55325,1.92716,5.58847,13.2627,-0.941604,-4.11195,-17.4149,-35.0507,-56.7481,+5919 more]
  NodeStressYZ = [0.224374,-0.625159,-0.880308,0.997506,-0.494682,0.855992,-0.617663,0.0624226,-0.862379,0.97045,2.54955,-3.59906,-1.49924,-2.0047,5.03428,3.50493,-0.134442,-0.584679,0.816981,3.63921,0.167652,0.862896,-15.3184,-17.836,-18.7001,-19.0526,+5920 more]
  NodeStressZZ = [-1.46908,-3.67498,-2.0787,-1.78839,6.94123,4.41685,6.22051,3.53012,-1.71062,-1.26658,-2.72764,-3.56141,1.4546,1.74786,-9.81132,4.04748,-0.184098,2.02697,0.761857,1.41685,0.675727,6.86657,-79.065,-48.9985,-44.1103,-30.2427,-10.1778,12.4548,+5918 more]
  PrincipalMax = [81.9468,86.1683,2.52645,2.20446,9.22953,8.28312,8.93071,6.43265,2.51638,2.34639,60.5801,60.4164,47.4001,17.4913,5.46166,9.2525,4.57129,5.38399,9.5398,14.5668,21.4537,28.4712,48.8385,55.414,32.8705,14.075,8.65848,16.2611,36.5258,83.5763,+5916 more]
  PrincipalMed = [0.268748,-1.55271,0.0131155,0.0141539,-1.24527,0.0411952,-0.51094,-1.07498,0.0270233,0.0298739,-1.98455,-1.36508,4.76669,2.97761,-0.0353935,-0.0133637,-0.0813314,0.785267,0.334112,-1.96899,3.48219,8.32647,-4.56193,1.5775,-7.8463,-23.2112,+5920 more]
  PrincipalMin = [-1.58914,-4.3141,-4.23156,-3.98841,-2.13945,-5.48749,-3.66513,-3.21683,-3.23513,-2.69843,-5.64019,-7.12424,0.762876,-0.222154,-13.5823,-8.22712,-21.537,-92.9885,-200.172,-383.439,-670.843,-1033.73,-1523.7,-2141.02,-2823.78,-3528.27,+5920 more]
  ResultType = Fem::ResultMechanical
  Stats = [-42.6844,29.8253,-3.92765,3.93459,-111.863,213.263,0.806372,213.294,3.7953,4746.69,-82.9821,4792.26,-782.611,801.399,-4729.42,88.0078,2.17473,2400.21,0,0,0,0,0,0,0,0]
  Time = 0
  vonMises = [82.6227,89.1338,5.91628,5.43919,10.9493,12.0026,11.3523,8.7768,4.99592,4.37379,64.4702,64.8531,44.7698,16.3501,16.9766,15.1469,24.1209,96.1557,205.264,390.001,683.488,1052.27,1546.53,2170.02,2836.51,3523.85,4089,4332.42,4044.61,3134.2,+5916 more]
FEATURE [Fem::FemResultObjectPython] CCX_EigenMode_12_Results  # FEM object (typed FeaturePython)
  DisplacementLengths = [68.6825,68.6794,70.4286,70.4376,62.2603,62.2696,66.2944,66.2941,73.2368,73.2388,72.2587,72.2605,72.6775,73.0023,66.9255,63.9525,65.5463,64.6471,63.4084,61.6079,58.9394,54.847,48.7559,39.6913,26.9666,14.558,30.4436,67.1448,115.21,171.456,+5916 more]
  DisplacementVectors = (5946) [(1.10693,34.6241,-59.3062),(-1.10197,34.6194,59.3055),(1.21312,36.0292,-60.503),(-1.20752,36.0299,60.5132),(2.56965,-14.4649,-60.5021),+5941 more]
  Eigenmode = 12
  EigenmodeFrequency = 1821.99
  MaxShear = [67.1035,64.1939,6.14657,5.20353,10.3253,11.4864,12.4372,13.7859,7.61105,7.48886,77.498,79.0024,54.6978,13.3493,19.2994,14.8891,37.9595,120.846,217.894,342.827,500.732,684.832,919.199,1245.45,1607.5,2001.08,2387.35,2713.8,2940.91,3064.92,+5916 more]
  Mesh = -> ResultMesh
  NodeNumbers = <same value as first occurrence — deduplicated (x6 in doc)>
  NodeStrainXX = [0.0144731,-0.0135291,-0.000392336,0.000370678,0.000515251,-0.00109016,0.00082505,-0.00160861,-0.000516915,0.000531286,0.0165749,-0.0168349,0.0116519,0.00211934,-0.000922977,0.000845393,-0.00720032,-0.0270294,-0.0500085,-0.0783699,-0.112641,+5925 more]
  NodeStrainXY = [0.00232406,0.00304784,-0.000592495,-0.000504406,0.000511325,0.000739536,-0.000619302,-0.00115243,0.000725651,0.000758347,-0.00160892,-0.00197214,-0.00328866,-0.00104456,0.00139585,-0.000452104,0.00352734,0.00500637,0.00700461,0.0108467,+5926 more]
  NodeStrainXZ = [-0.00351119,0.00400049,0.000116646,-7.23887e-05,0.000120368,-6.03623e-05,0.000116057,-0.000283473,1.73874e-05,-0.000114408,0.00549988,-0.00560777,0.0010604,2.4041e-05,-0.000531154,-0.00105871,0.000909471,0.00241123,0.00388731,0.00797089,+5926 more]
  NodeStrainYY = [-0.00514722,0.00453861,-0.000249434,0.000214947,0.000722307,-0.00038359,0.000628396,-6.23541e-05,-0.000251112,0.000250469,-0.00584607,0.00598528,-0.00393178,-0.000311908,-0.00148562,0.000646403,0.00142925,0.00892137,0.0159357,0.0250669,+5926 more]
  NodeStrainYZ = [-0.000226324,-0.000638746,-0.000482633,-0.000382792,-0.00102012,-0.000866938,-0.00131218,-0.000945517,-0.000673168,-0.00064396,-0.000510676,-0.000476265,-0.000190016,-0.0011071,0.00163092,0.00134563,-0.000940463,-0.000573007,-0.000263743,+5927 more]
  NodeStrainZZ = [-0.00409521,0.00401858,0.000641025,-0.000558262,-0.0013961,0.0015902,-0.00155866,0.00145163,0.000714867,-0.000638234,-0.00446849,0.00459314,-0.00348794,-0.000324141,0.00227182,-0.00191073,0.00243889,0.00822119,0.015845,0.0248417,0.0363973,+5925 more]
  NodeStressXX = [123.138,-115.578,-2.53066,2.54356,2.41043,-6.35337,4.71057,-11.6139,-3.6329,4.24267,142.566,-144.218,99.2563,22.1375,-6.72627,3.04585,-65.4388,-230.644,-426.359,-667.564,-959.482,-1307.43,-1549.69,-2022.58,-2471.58,-2825.02,-2925.38,+5919 more]
  NodeStressXY = [14.9656,19.6263,-3.81531,-3.24807,3.29262,4.76217,-3.98793,-7.42094,4.67275,4.8833,-10.3605,-12.6994,-21.177,-6.7263,8.98843,-2.91128,22.7139,32.238,45.1054,69.8462,127.352,203.293,365.939,550.309,794.842,1118.04,1514.48,1946.31,2333.99,+5917 more]
  NodeStressXZ = [-22.6099,25.7608,0.751129,-0.466139,0.775099,-0.388696,0.747338,-1.82539,0.111965,-0.73672,35.4159,-36.1106,6.82831,0.15481,-3.42031,-6.81748,5.85644,15.5268,25.0319,51.3277,78.55,111.046,280.542,405.63,580.262,804.012,1070.49,1343.69,+5918 more]
  NodeStressYY = [-3.20524,0.767251,-1.61046,1.54075,3.74374,-1.80352,3.44424,-1.65696,-1.92129,2.43438,-1.81172,2.72996,-1.09343,6.48174,-10.3493,1.76447,-9.86957,0.856984,-1.71805,-1.49354,-6.5832,-21.7626,-22.3786,-22.4152,-32.6642,-43.3268,-51.8426,+5919 more]
  NodeStressYZ = [-1.45739,-4.11314,-3.10787,-2.46495,-6.56895,-5.58256,-8.44963,-6.08856,-4.3348,-4.14671,-3.28844,-3.06686,-1.22359,-7.12904,10.5022,8.66506,-6.05601,-3.68982,-1.69835,-2.6259,0.463832,-5.81593,32.7553,51.984,66.0329,78.8658,86.8734,+5919 more]
  NodeStressZZ = [3.56905,-2.58144,4.12356,-3.43825,-9.89751,10.9065,-10.6391,8.09216,4.29903,-3.28834,7.05904,-6.23461,1.76462,6.40296,13.8463,-14.7019,-3.36812,-3.65171,-2.30253,-2.94365,0.236178,2.50506,38.8125,44.808,54.7455,64.2572,70.9327,72.2708,+5918 more]
  PrincipalMax = [128.969,4.00126,6.13707,5.51813,7.84748,13.2359,10.2227,11.1451,6.98252,9.18336,152.029,3.82014,104.013,25.0459,17.7691,10.1413,1.57194,5.55822,3.23012,6.94732,19.0906,21.7905,164.036,263.118,405.784,626.208,962.979,1460.62,2152.88,3023.66,+5916 more]
  PrincipalMed = [-0.229846,2.9931,0.0014398,0.0168508,1.21232,-0.749342,1.94477,0.102756,0.00188942,-0.000276006,-1.24792,2.64182,1.2978,11.6289,-0.168628,-0.395965,-5.90141,-2.86222,-1.05142,-0.240835,-2.54701,-0.604097,-22.9303,-35.5248,-46.072,-54.3553,+5920 more]
  PrincipalMin = [-5.2377,-124.387,-6.15607,-4.88892,-12.8031,-9.73694,-14.6518,-16.4266,-8.23957,-5.79437,-2.96735,-154.185,-5.38299,-1.65263,-20.8297,-19.6369,-74.347,-236.135,-432.558,-678.708,-982.373,-1347.87,-1674.36,-2227.78,-2809.21,-3375.94,+5920 more]
  ResultType = Fem::ResultMechanical
  Stats = [-23.7483,23.7655,-51.9779,36.3764,-388.403,388.411,0.168531,391.368,7.01196,6755.06,-171.014,5468.39,-1126.31,1111.88,-5499.08,131.063,3.98911,3884.89,0,0,0,0,0,0,0,0]
  Time = 0
  vonMises = [131.775,127.887,10.6462,9.01769,18.2607,20.0514,21.9398,24.0349,13.1978,13.0813,154.143,157.419,106.213,23.1217,33.4552,26.1533,72.4719,237.595,433.663,682.089,990.822,1358.61,1752.41,2355.82,3014.57,3709,4355.06,4852.12,5149.75,5308.7,+5916 more]
FEATURE [App::TextDocument] ccx_dat_file
  Text = <blob: 3833 chars omitted>
FEATURE [Fem::FemAnalysis] Analysis
  Group = -> [SolverCcxTools,MaterialSolid,FemConstraintDisplacement,FEMMeshNetgen,CCX_EigenMode_7_Results,CCX_EigenMode_8_Results,CCX_EigenMode_9_Results,CCX_EigenMode_10_Results,CCX_EigenMode_11_Results,CCX_EigenMode_12_Results,ccx_dat_file]
